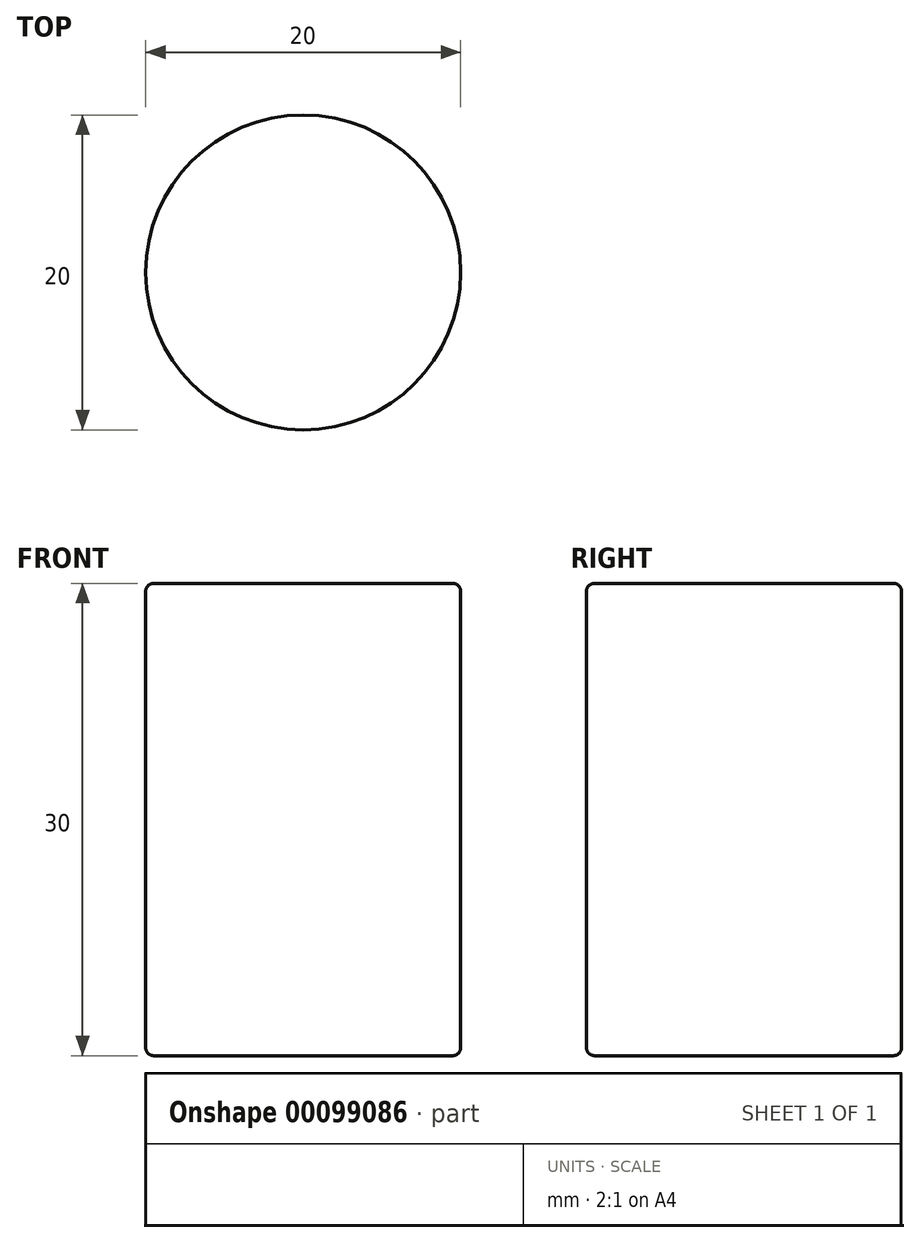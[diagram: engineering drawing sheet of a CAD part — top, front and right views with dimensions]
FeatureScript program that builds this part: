
annotation { "Feature Type Name" : "Feature", "Feature Type Description" : "" }
export const myFeature = defineFeature(function(context is Context, id is Id, definition is map)
    precondition{}
    {
        {
            var Q0;
            Q0=qCreatedBy(makeId("Top.planeOp"),FACE);
            var sketch = newSketch(context, id + "F0", { "sketchPlane" : qUnion([Q0])});
            skCircle(sketch, "E0", {"center": v(0, 0) * mm, "radius": 10 * mm});
            skSolve(sketch);
        }
        {
            var Q0;
            Q0=makeQuery(id+"F0.imprint","IMPRINT",FACE,{"disambiguationData":[TD([[makeQuery(id+"F0.imprint","IMPRINT",EDGE,{"derivedFrom":sQuery(id+"F0.wireOp",EDGE,"E0")}),1.0]])]});
            extrude(context, id + "F1", {"entities" : qUnion([Q0]), "depth" : 30 * mm});
        }
        {
            var Q0;
            Q0=makeQuery(id+"F1.opExtrude","CAP_EDGE",EDGE,{"disambiguationData":[OSD([sQuery(id+"F0.wireOp",EDGE,"E0")])],"isStart":true});
            var Q1;
            Q1=makeQuery(id+"F1.opExtrude","CAP_EDGE",EDGE,{"disambiguationData":[OSD([sQuery(id+"F0.wireOp",EDGE,"E0")])],"isStart":false});
            fillet(context, id + "F2", {"entities" : qUnion([Q0, Q1]), "radius" : 0.5 * mm, "tangentPropagation" : true, "allowEdgeOverflow" : false});
        }
    });
